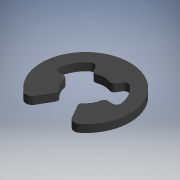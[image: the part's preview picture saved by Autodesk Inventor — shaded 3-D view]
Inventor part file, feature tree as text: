
AUTODESK INVENTOR PART (.ipt)
format: ipt  version: 2017.3 (Build 213256000, 256)  size: 128,000 bytes
history: native  units: mm (DEFAULTED — no unit token found)
features: other x7, extrude x1, sketch x1
ambient origin geometry x8: Origin, YZ Plane, XZ Plane, XY Plane, X Axis, Y Axis, Z Axis, Center Point
bodies: Solid1 (feature_tree)
feature tree (9):
  extrude  "Extrusion1"  [1 undecoded]
  other  "RR_XY"
  other  "RR_YZ"
  other  "RR_ZX"
  other  "RR_X"
  other  "RR_Y"
  other  "RR_Z"
  other  "RR_Center"
  sketch  "Sketch_1"  dims[d0=1.1049mm d1=0.0mm]
note: 1 required parameter value undecoded (feature->parameter linkage not recoverable at this tier; creation-order binding heuristic only, values carry confidence <= 0.55)
